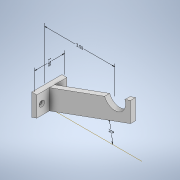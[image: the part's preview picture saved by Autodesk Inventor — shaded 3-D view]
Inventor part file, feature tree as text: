
AUTODESK INVENTOR PART (.ipt)
format: ipt  version: 2021.1 (Build 251245010, 245A)  size: 340,992 bytes
history: native  units: in
note: dims shown in document units (in); Inventor stores cm internally (conversion verified against a paired STEP export)
features: sketch x5, other x4, extrude x4, hole x1
ambient origin geometry x8: Origin, YZ Plane, XZ Plane, XY Plane, X Axis, Y Axis, Z Axis, Center Point
bodies: Solid2 (feature_tree)
feature tree (14):
  other  "Annotations"
  extrude  "Extrusion3"  Depth=0.25in
  extrude  "Extrusion4"  Depth=0.1374in
  sketch  "Sketch7"  dims[d26=1.075in d29=0.25in]
  extrude  "Extrusion5"  Depth=0.25in
  hole  "Hole3"  [1 undecoded]
  extrude  "Extrusion6"  TaperAngle=0.0deg  [1 undecoded]
  sketch  "Sketch5"  dims[d21=1.0in d22=0.25in]
  sketch  "Sketch6"  dims[d23=1.5in d24=0.0in d25=0.1374in]
  sketch  "Sketch8"  dims[d30=3.5in d31=0.25in]
  sketch  "Sketch9"  dims[d32=0.0in d33=0.0in d34=0.25in d35=0.25in d47=1.5in d48=0.0in d49=0.15in d50=0.75in d51=0.279in d52=0.25in d53=0.5635in d54=1.0in d55=0.8108in d63=0.05in d64=0.0in d56=0.2085in d57=0.331in d58=1.5in d59=2.3174in d60=0.1374in d62=3.5in]
  other  "Linear Dimension 1"
  other  "Angular Dimension 1"
  other  "Linear Dimension 3"
note: 2 required parameter values undecoded (feature->parameter linkage not recoverable at this tier; creation-order binding heuristic only, values carry confidence <= 0.55)
